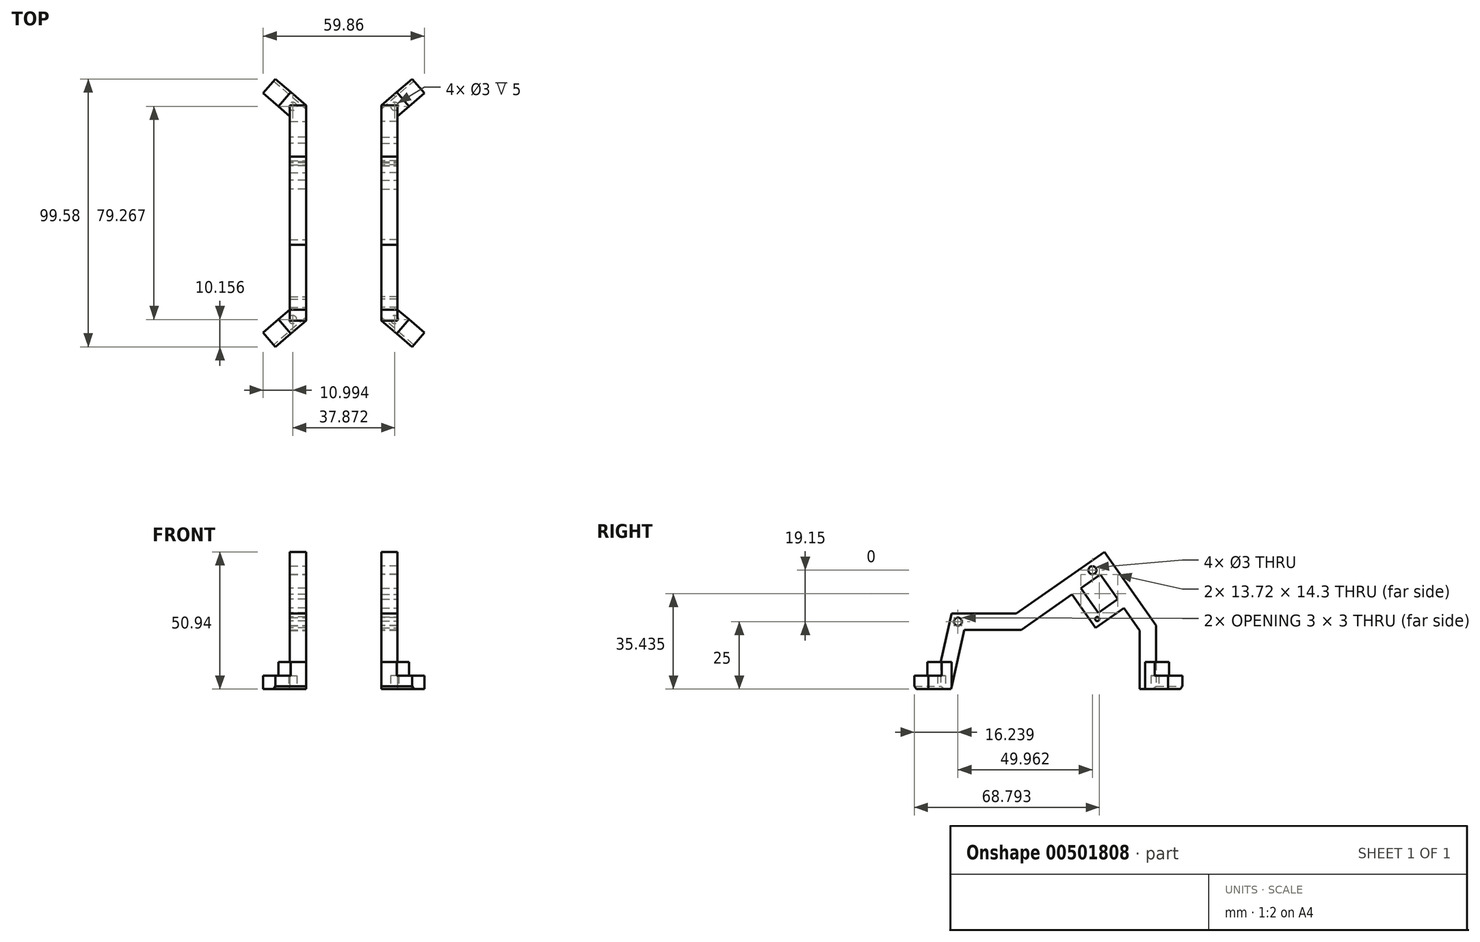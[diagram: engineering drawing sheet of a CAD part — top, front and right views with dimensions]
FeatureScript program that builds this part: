
annotation { "Feature Type Name" : "Feature", "Feature Type Description" : "" }
export const myFeature = defineFeature(function(context is Context, id is Id, definition is map)
    precondition{}
    {
        {
            var Q0;
            Q0=qCreatedBy(makeId("Top.planeOp"),FACE);
            var sketch = newSketch(context, id + "F0", { "sketchPlane" : qUnion([Q0])});
            skLineSegment(sketch, "E0", {"start": v(14, 40) * mm, "end": v(25.36, 49.8) * mm});
            skLineSegment(sketch, "E1", {"start": v(25.36, 49.8) * mm, "end": v(29.93, 44.5) * mm});
            skLineSegment(sketch, "E2", {"start": v(29.93, 44.5) * mm, "end": v(18.57, 34.7) * mm});
            skLineSegment(sketch, "E3", {"start": v(14, 40) * mm, "end": v(0, 40) * mm, "construction": true});
            skLineSegment(sketch, "E4", {"start": v(0, 40) * mm, "end": v(0, 0) * mm, "construction": true});
            skLineSegment(sketch, "E5", {"start": v(14, 40) * mm, "end": v(18.57, 34.7) * mm});
            skCircle(sketch, "E6", {"center": v(18.94, 39.63) * mm, "radius": 1.5 * mm});
            skLineSegment(sketch, "E7", {"start": v(14, 40) * mm, "end": v(20, 40) * mm});
            skLineSegment(sketch, "E8", {"start": v(20, 40) * mm, "end": v(20, 0) * mm});
            skLineSegment(sketch, "E9", {"start": v(14, 40) * mm, "end": v(14, 0) * mm});
            skLineSegment(sketch, "E10", {"start": v(19.68, 44.9) * mm, "end": v(24.25, 39.6) * mm});
            skLineSegment(sketch, "E11.MirrorCS", {"start": v(19.68, -44.9) * mm, "end": v(24.25, -39.6) * mm});
            skLineSegment(sketch, "E12.MirrorCS", {"start": v(14, -40) * mm, "end": v(20, -40) * mm});
            skCircle(sketch, "E13.MirrorC", {"center": v(18.94, -39.63) * mm, "radius": 1.5 * mm});
            skLineSegment(sketch, "E14.MirrorCS", {"start": v(14, -40) * mm, "end": v(18.57, -34.7) * mm});
            skLineSegment(sketch, "E15.MirrorCS", {"start": v(14, -40) * mm, "end": v(14, 0) * mm});
            skLineSegment(sketch, "E16.MirrorCS", {"start": v(20, -40) * mm, "end": v(20, 0) * mm});
            skLineSegment(sketch, "E17.MirrorCS", {"start": v(14, -40) * mm, "end": v(0, -40) * mm, "construction": true});
            skLineSegment(sketch, "E18.MirrorCS", {"start": v(0, -40) * mm, "end": v(0, 0) * mm, "construction": true});
            skLineSegment(sketch, "E19.MirrorCS", {"start": v(29.93, -44.5) * mm, "end": v(18.57, -34.7) * mm});
            skLineSegment(sketch, "E20.MirrorCS", {"start": v(25.36, -49.8) * mm, "end": v(29.93, -44.5) * mm});
            skLineSegment(sketch, "E21.MirrorCS", {"start": v(14, -40) * mm, "end": v(25.36, -49.8) * mm});
            skSolve(sketch);
        }
        {
            var Q0;
            {var subQ1=sQuery(id+"F0.wireOp",EDGE,"E5");Q0=makeQuery(id+"F0.imprint","IMPRINT",FACE,{"disambiguationData":[TD([[makeQuery(id+"F0.imprint","IMPRINT",EDGE,{"derivedFrom":subQ1}),1.0]])]});}
            var Q1;
            {var subQ0=sQuery(id+"F0.wireOp",EDGE,"E7");var subQ1=sQuery(id+"F0.wireOp",EDGE,"E6");var subQ2=makeQuery(id+"F0.imprint","INTERSECT",VERTEX,{"derivedFrom":[subQ1,subQ0]});Q1=makeQuery(id+"F0.imprint","IMPRINT",FACE,{"disambiguationData":[TD([[makeQuery(id+"F0.imprint","IMPRINT",EDGE,{"disambiguationData":[TD([[subQ2,-1.0]])],"derivedFrom":subQ1}),1.0]])]});}
            var Q2;
            {var subQ7=sQuery(id+"F0.wireOp",EDGE,"E5");Q2=makeQuery(id+"F0.imprint","IMPRINT",FACE,{"disambiguationData":[TD([[makeQuery(id+"F0.imprint","IMPRINT",EDGE,{"derivedFrom":subQ7}),-1.0]])]});}
            var Q3;
            {var subQ0=sQuery(id+"F0.wireOp",EDGE,"E14.MirrorCS");Q3=makeQuery(id+"F0.imprint","IMPRINT",FACE,{"disambiguationData":[TD([[makeQuery(id+"F0.imprint","IMPRINT",EDGE,{"derivedFrom":subQ0}),-1.0]])]});}
            var Q4;
            {var subQ0=sQuery(id+"F0.wireOp",EDGE,"E16.MirrorCS");var subQ1=sQuery(id+"F0.wireOp",EDGE,"E12.MirrorCS");var subQ2=makeQuery(id+"F0.imprint","INTERSECT",VERTEX,{"derivedFrom":[subQ1,subQ0]});Q4=makeQuery(id+"F0.imprint","IMPRINT",FACE,{"disambiguationData":[TD([[makeQuery(id+"F0.imprint","IMPRINT",EDGE,{"disambiguationData":[TD([[subQ2,1.0]])],"derivedFrom":subQ1}),1.0]])]});}
            extrude(context, id + "F1", {"entities" : qUnion([Q0, Q1, Q2, Q3, Q4]), "depth" : 70 * mm});
        }
        {
            var Q0;
            {var subQ0=sQuery(id+"F0.wireOp",EDGE,"E7");var subQ1=sQuery(id+"F0.wireOp",EDGE,"E6");var subQ2=makeQuery(id+"F0.imprint","INTERSECT",VERTEX,{"derivedFrom":[subQ1,subQ0]});Q0=makeQuery(id+"F0.imprint","IMPRINT",FACE,{"disambiguationData":[TD([[makeQuery(id+"F0.imprint","IMPRINT",EDGE,{"disambiguationData":[TD([[subQ2,1.0]])],"derivedFrom":subQ1}),1.0]])]});}
            var Q1;
            {var subQ7=sQuery(id+"F0.wireOp",EDGE,"E10");Q1=makeQuery(id+"F0.imprint","IMPRINT",FACE,{"disambiguationData":[TD([[makeQuery(id+"F0.imprint","IMPRINT",EDGE,{"derivedFrom":subQ7}),-1.0]])]});}
            var Q2;
            {var subQ9=sQuery(id+"F0.wireOp",EDGE,"E11.MirrorCS");Q2=makeQuery(id+"F0.imprint","IMPRINT",FACE,{"disambiguationData":[TD([[makeQuery(id+"F0.imprint","IMPRINT",EDGE,{"derivedFrom":subQ9}),1.0]])]});}
            var Q3;
            {var subQ0=sQuery(id+"F0.wireOp",EDGE,"E16.MirrorCS");var subQ1=sQuery(id+"F0.wireOp",EDGE,"E12.MirrorCS");var subQ2=makeQuery(id+"F0.imprint","INTERSECT",VERTEX,{"derivedFrom":[subQ1,subQ0]});Q3=makeQuery(id+"F0.imprint","IMPRINT",FACE,{"disambiguationData":[TD([[makeQuery(id+"F0.imprint","IMPRINT",EDGE,{"disambiguationData":[TD([[subQ2,1.0]])],"derivedFrom":subQ1}),-1.0]])]});}
            extrude(context, id + "F2", {"entities" : qUnion([Q0, Q1, Q2, Q3]), "operationType" : NewBodyOperationType.ADD, "depth" : 10 * mm});
        }
        {
            var Q0;
            {var subQ0=sQuery(id+"F0.wireOp",EDGE,"E1");Q0=makeQuery(id+"F0.imprint","IMPRINT",FACE,{"disambiguationData":[TD([[makeQuery(id+"F0.imprint","IMPRINT",EDGE,{"derivedFrom":subQ0}),-1.0]])]});}
            var Q1;
            {var subQ0=sQuery(id+"F0.wireOp",EDGE,"E11.MirrorCS");Q1=makeQuery(id+"F0.imprint","IMPRINT",FACE,{"disambiguationData":[TD([[makeQuery(id+"F0.imprint","IMPRINT",EDGE,{"derivedFrom":subQ0}),-1.0]])]});}
            extrude(context, id + "F3", {"entities" : qUnion([Q0, Q1]), "operationType" : NewBodyOperationType.ADD, "depth" : 5 * mm});
        }
        {
            var Q0;
            Q0=makeQuery(id+"F1.opExtrude","SWEPT_FACE",FACE,{"disambiguationData":[OSD([sQuery(id+"F0.wireOp",EDGE,"E9"),sQuery(id+"F0.wireOp",EDGE,"E15.MirrorCS")])]});
            var sketch = newSketch(context, id + "F4", { "sketchPlane" : qUnion([Q0])});
            skLineSegment(sketch, "E22", {"start": v(0, 0) * mm, "end": v(0, 28) * mm, "construction": true});
            skPoint(sketch, "E22.endSnap0", {"position": v(0, 0) * mm});
            skLineSegment(sketch, "E23", {"start": v(-20.33, 28) * mm, "end": v(19.67, 28) * mm, "construction": true});
            skLineSegment(sketch, "E24", {"start": v(11.88, 28) * mm, "end": v(-20.88, 50.94) * mm});
            skLineSegment(sketch, "E25", {"start": v(40, 10) * mm, "end": v(35.95, 28) * mm});
            skLineSegment(sketch, "E26", {"start": v(35.95, 28) * mm, "end": v(11.88, 28) * mm});
            skLineSegment(sketch, "E27", {"start": v(-20.88, 50.94) * mm, "end": v(-40, 23.64) * mm});
            skLineSegment(sketch, "E28", {"start": v(-40, 23.64) * mm, "end": v(-40, 0) * mm});
            skLineSegment(sketch, "E29", {"start": v(36.1, 0) * mm, "end": v(31.15, 22) * mm});
            skLineSegment(sketch, "E30", {"start": v(31.15, 22) * mm, "end": v(10, 22) * mm});
            skLineSegment(sketch, "E31", {"start": v(10, 22) * mm, "end": v(-19.4, 42.59) * mm});
            skLineSegment(sketch, "E32", {"start": v(-19.4, 42.59) * mm, "end": v(-34, 21.75) * mm});
            skLineSegment(sketch, "E33", {"start": v(-34, 21.75) * mm, "end": v(-34, 0) * mm});
            skSolve(sketch);
        }
        {
            var Q0;
            {var subQ0=sQuery(id+"F4.wireOp",EDGE,"E29");Q0=makeQuery(id+"F4.imprint","IMPRINT",FACE,{"disambiguationData":[TD([[makeQuery(id+"F4.imprint","IMPRINT",EDGE,{"derivedFrom":subQ0}),1.0]])]});}
            var Q1;
            Q1=makeQuery(id+"F4.imprint","IMPRINT",FACE,{"disambiguationData":[TD([[makeQuery(id+"F4.imprint","IMPRINT",EDGE,{"derivedFrom":sQuery(id+"F4.wireOp",EDGE,"E24")}),-1.0]])]});
            extrude(context, id + "F5", {"entities" : qUnion([Q0, Q1]), "operationType" : NewBodyOperationType.REMOVE, "oppositeDirection" : true, "depth" : 25 * mm});
        }
        {
            var Q0;
            {var subQ0=sQuery(id+"F0.wireOp",EDGE,"E16.MirrorCS");var subQ1=sQuery(id+"F0.wireOp",EDGE,"E12.MirrorCS");var subQ2=makeQuery(id+"F0.imprint","INTERSECT",VERTEX,{"derivedFrom":[subQ1,subQ0]});Q0=makeQuery(id+"F0.imprint","IMPRINT",FACE,{"disambiguationData":[TD([[makeQuery(id+"F0.imprint","IMPRINT",EDGE,{"disambiguationData":[TD([[subQ2,1.0]])],"derivedFrom":subQ1}),-1.0]])]});}
            var Q1;
            {var subQ0=sQuery(id+"F0.wireOp",EDGE,"E16.MirrorCS");var subQ1=sQuery(id+"F0.wireOp",EDGE,"E12.MirrorCS");var subQ2=makeQuery(id+"F0.imprint","INTERSECT",VERTEX,{"derivedFrom":[subQ1,subQ0]});Q1=makeQuery(id+"F0.imprint","IMPRINT",FACE,{"disambiguationData":[TD([[makeQuery(id+"F0.imprint","IMPRINT",EDGE,{"disambiguationData":[TD([[subQ2,1.0]])],"derivedFrom":subQ1}),1.0]])]});}
            var Q2;
            {var subQ0=sQuery(id+"F0.wireOp",EDGE,"E7");var subQ1=sQuery(id+"F0.wireOp",EDGE,"E6");var subQ2=makeQuery(id+"F0.imprint","INTERSECT",VERTEX,{"derivedFrom":[subQ1,subQ0]});Q2=makeQuery(id+"F0.imprint","IMPRINT",FACE,{"disambiguationData":[TD([[makeQuery(id+"F0.imprint","IMPRINT",EDGE,{"disambiguationData":[TD([[subQ2,1.0]])],"derivedFrom":subQ1}),1.0]])]});}
            var Q3;
            {var subQ0=sQuery(id+"F0.wireOp",EDGE,"E7");var subQ1=sQuery(id+"F0.wireOp",EDGE,"E6");var subQ2=makeQuery(id+"F0.imprint","INTERSECT",VERTEX,{"derivedFrom":[subQ1,subQ0]});Q3=makeQuery(id+"F0.imprint","IMPRINT",FACE,{"disambiguationData":[TD([[makeQuery(id+"F0.imprint","IMPRINT",EDGE,{"disambiguationData":[TD([[subQ2,-1.0]])],"derivedFrom":subQ1}),1.0]])]});}
            extrude(context, id + "F6", {"entities" : qUnion([Q0, Q1, Q2, Q3]), "operationType" : NewBodyOperationType.REMOVE, "depth" : 5 * mm});
        }
        {
            var Q0;
            Q0=makeQuery(id+"F1.opExtrude","SWEPT_FACE",FACE,{"disambiguationData":[OSD([sQuery(id+"F0.wireOp",EDGE,"E9"),sQuery(id+"F0.wireOp",EDGE,"E15.MirrorCS")])]});
            var sketch = newSketch(context, id + "F7", { "sketchPlane" : qUnion([Q0])});
            skCircle(sketch, "E34", {"center": v(-16.41, 44.15) * mm, "radius": 1.5 * mm});
            skLineSegment(sketch, "E35", {"start": v(35.95, 28) * mm, "end": v(31.15, 22) * mm, "construction": true});
            skCircle(sketch, "E36", {"center": v(33.55, 25) * mm, "radius": 1.5 * mm});
            skLineSegment(sketch, "E37", {"start": v(35.95, 28) * mm, "end": v(31.94, 28) * mm, "construction": true});
            skLineSegment(sketch, "E38", {"start": v(-16.41, 44.15) * mm, "end": v(-14.69, 46.6) * mm, "construction": true});
            skLineSegment(sketch, "E39", {"start": v(-14.69, 46.6) * mm, "end": v(-20.88, 50.94) * mm, "construction": true});
            skLineSegment(sketch, "E40", {"start": v(-16.41, 44.15) * mm, "end": v(-18.13, 41.7) * mm, "construction": true});
            skSolve(sketch);
        }
        {
            var Q0;
            Q0=makeQuery(id+"F1.opExtrude","SWEPT_FACE",FACE,{"disambiguationData":[OSD([sQuery(id+"F0.wireOp",EDGE,"E8"),sQuery(id+"F0.wireOp",EDGE,"E16.MirrorCS")])]});
            var sketch = newSketch(context, id + "F8", { "sketchPlane" : qUnion([Q0])});
            skLineSegment(sketch, "E41", {"start": v(8.87, 35.2) * mm, "end": v(17.61, 22.71) * mm});
            skLineSegment(sketch, "E42", {"start": v(28.16, 30.1) * mm, "end": v(17.61, 22.71) * mm});
            skLineSegment(sketch, "E43", {"start": v(18.6, 28.28) * mm, "end": v(25.86, 33.37) * mm});
            skLineSegment(sketch, "E44", {"start": v(18.6, 28.28) * mm, "end": v(12.14, 37.5) * mm});
            skLineSegment(sketch, "E45", {"start": v(18.6, 28.28) * mm, "end": v(17.61, 22.71) * mm, "construction": true});
            skCircle(sketch, "E46", {"center": v(18.2, 25.99) * mm, "radius": 0.77 * mm});
            skSolve(sketch);
        }
        {
            var Q0;
            {var subQ5=sQuery(id+"F8.wireOp",EDGE,"E41");Q0=makeQuery(id+"F8.imprint","IMPRINT",FACE,{"disambiguationData":[TD([[makeQuery(id+"F8.imprint","IMPRINT",EDGE,{"derivedFrom":subQ5}),1.0]])]});}
            extrude(context, id + "F9", {"entities" : qUnion([Q0]), "oppositeDirection" : true, "depth" : 6 * mm});
        }
        {
            var Q0;
            Q0=makeQuery(id+"F7.imprint","IMPRINT",FACE,{"disambiguationData":[TD([[makeQuery(id+"F7.imprint","IMPRINT",EDGE,{"derivedFrom":sQuery(id+"F7.wireOp",EDGE,"E34")}),1.0]])]});
            extrude(context, id + "F10", {"entities" : qUnion([Q0]), "operationType" : NewBodyOperationType.REMOVE, "oppositeDirection" : true, "depth" : 7 * mm});
        }
        {
            var Q0;
            Q0=makeQuery(id+"F9.opExtrude","SWEPT_BODY",BODY,{"disambiguationData":[OSD([sQuery(id+"F0.wireOp",EDGE,"E8"),sQuery(id+"F0.wireOp",EDGE,"E16.MirrorCS"),sQuery(id+"F4.wireOp",EDGE,"E31"),sQuery(id+"F4.wireOp",EDGE,"E32"),sQuery(id+"F8.wireOp",EDGE,"E41"),sQuery(id+"F8.wireOp",EDGE,"E42"),sQuery(id+"F8.wireOp",EDGE,"E43"),sQuery(id+"F8.wireOp",EDGE,"E44"),sQuery(id+"F8.wireOp",EDGE,"E46")])]});
            var Q1;
            Q1=makeQuery(id+"F1.opExtrude","SWEPT_BODY",BODY,{"disambiguationData":[OSD([sQuery(id+"F0.wireOp",EDGE,"E7"),sQuery(id+"F0.wireOp",EDGE,"E8"),sQuery(id+"F0.wireOp",EDGE,"E9"),sQuery(id+"F0.wireOp",EDGE,"E12.MirrorCS"),sQuery(id+"F0.wireOp",EDGE,"E15.MirrorCS"),sQuery(id+"F0.wireOp",EDGE,"E16.MirrorCS")])]});
            booleanBodies(context, id + "F11", {"operationType" : BooleanOperationType.UNION, "tools" : qUnion([Q0, Q1])});
        }
        {
            var Q0;
            Q0=makeQuery(id+"F9.opExtrude","SWEPT_BODY",BODY,{"disambiguationData":[OSD([sQuery(id+"F0.wireOp",EDGE,"E8"),sQuery(id+"F0.wireOp",EDGE,"E16.MirrorCS"),sQuery(id+"F4.wireOp",EDGE,"E31"),sQuery(id+"F4.wireOp",EDGE,"E32"),sQuery(id+"F8.wireOp",EDGE,"E41"),sQuery(id+"F8.wireOp",EDGE,"E42"),sQuery(id+"F8.wireOp",EDGE,"E43"),sQuery(id+"F8.wireOp",EDGE,"E44"),sQuery(id+"F8.wireOp",EDGE,"E46")])]});
            var Q1;
            Q1=qCreatedBy(makeId("Right.planeOp"),FACE);
            mirror(context, id + "F12", {"entities" : qUnion([Q0]), "mirrorPlane" : qUnion([Q1])});
        }
        {
            var Q0;
            Q0=makeQuery(id+"F7.imprint","IMPRINT",FACE,{"disambiguationData":[TD([[makeQuery(id+"F7.imprint","IMPRINT",EDGE,{"derivedFrom":sQuery(id+"F7.wireOp",EDGE,"E36")}),1.0]])]});
            var Q1;
            Q1=sQuery(id+"F7.wireOp",EDGE,"E36");
            extrude(context, id + "F13", {"entities" : qUnion([Q0]), "operationType" : NewBodyOperationType.REMOVE, "surfaceEntities" : qUnion([Q1]), "endBound" : BoundingType.SYMMETRIC, "oppositeDirection" : true, "depth" : 12 * mm});
        }
        {
            var Q0;
            Q0=makeQuery(id+"F12.opPattern","COPY",FACE,{"derivedFrom":makeQuery(id+"F11.opBoolean","MERGE",FACE,{"derivedFrom":[makeQuery(id+"F9.opExtrude","CAP_FACE",FACE,{"disambiguationData":[OSD([sQuery(id+"F0.wireOp",EDGE,"E8"),sQuery(id+"F0.wireOp",EDGE,"E16.MirrorCS"),sQuery(id+"F4.wireOp",EDGE,"E31"),sQuery(id+"F4.wireOp",EDGE,"E32"),sQuery(id+"F8.wireOp",EDGE,"E41"),sQuery(id+"F8.wireOp",EDGE,"E42"),sQuery(id+"F8.wireOp",EDGE,"E43"),sQuery(id+"F8.wireOp",EDGE,"E44"),sQuery(id+"F8.wireOp",EDGE,"E46")])],"isStart":false}),makeQuery(id+"F1.opExtrude","SWEPT_FACE",FACE,{"disambiguationData":[OSD([sQuery(id+"F0.wireOp",EDGE,"E9"),sQuery(id+"F0.wireOp",EDGE,"E15.MirrorCS")])]})]}),"instanceName":"1"});
            var sketch = newSketch(context, id + "F14", { "sketchPlane" : qUnion([Q0])});
            skLineSegment(sketch, "E47", {"start": v(-35.95, 28) * mm, "end": v(-31.15, 22) * mm, "construction": true});
            skCircle(sketch, "E48", {"center": v(-33.55, 25) * mm, "radius": 1.5 * mm});
            skSolve(sketch);
        }
        {
            var Q0;
            Q0=qSketchRegion(id+"F14",true);
            extrude(context, id + "F15", {"entities" : qUnion([Q0]), "operationType" : NewBodyOperationType.REMOVE, "oppositeDirection" : true, "depth" : 12 * mm});
        }
        {
            var Q0;
            {var subQ0=sQuery(id+"F0.wireOp",EDGE,"E21.MirrorCS");Q0=makeQuery(id+"F12.opPattern","COPY",EDGE,{"derivedFrom":makeQuery(id+"F3.boolean.opBoolean","MERGE",EDGE,{"derivedFrom":[makeQuery(id+"F2.opExtrude","CAP_EDGE",EDGE,{"disambiguationData":[OSD([subQ0])],"isStart":true}),makeQuery(id+"F3.opExtrude","CAP_EDGE",EDGE,{"disambiguationData":[OSD([subQ0])],"isStart":true})]}),"instanceName":"1"});}
            var Q1;
            {var subQ0=sQuery(id+"F0.wireOp",EDGE,"E21.MirrorCS");Q1=makeQuery(id+"F3.boolean.opBoolean","MERGE",EDGE,{"derivedFrom":[makeQuery(id+"F2.opExtrude","CAP_EDGE",EDGE,{"disambiguationData":[OSD([subQ0])],"isStart":true}),makeQuery(id+"F3.opExtrude","CAP_EDGE",EDGE,{"disambiguationData":[OSD([subQ0])],"isStart":true})]});}
            var Q2;
            {var subQ0=sQuery(id+"F0.wireOp",EDGE,"E0");Q2=makeQuery(id+"F3.boolean.opBoolean","MERGE",EDGE,{"derivedFrom":[makeQuery(id+"F2.opExtrude","CAP_EDGE",EDGE,{"disambiguationData":[OSD([subQ0])],"isStart":true}),makeQuery(id+"F3.opExtrude","CAP_EDGE",EDGE,{"disambiguationData":[OSD([subQ0])],"isStart":true})]});}
            var Q3;
            {var subQ0=sQuery(id+"F0.wireOp",EDGE,"E0");Q3=makeQuery(id+"F12.opPattern","COPY",EDGE,{"derivedFrom":makeQuery(id+"F3.boolean.opBoolean","MERGE",EDGE,{"derivedFrom":[makeQuery(id+"F2.opExtrude","CAP_EDGE",EDGE,{"disambiguationData":[OSD([subQ0])],"isStart":true}),makeQuery(id+"F3.opExtrude","CAP_EDGE",EDGE,{"disambiguationData":[OSD([subQ0])],"isStart":true})]}),"instanceName":"1"});}
            chamfer(context, id + "F16", {"entities" : qUnion([Q0, Q1, Q2, Q3]), "width" : 1 * mm, "tangentPropagation" : true});
        }
    });
